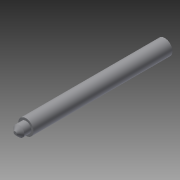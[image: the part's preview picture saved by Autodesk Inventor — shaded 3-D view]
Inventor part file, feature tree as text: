
AUTODESK INVENTOR PART (.ipt)
format: ipt  version: 2013 (Build 170138000, 138)  size: 76,800 bytes
history: native  units: in
note: dims shown in document units (in); Inventor stores cm internally (conversion verified against a paired STEP export)
features: extrude x2, sketch x2, chamfer x1
ambient origin geometry x8: Origin, YZ Plane, XZ Plane, XY Plane, X Axis, Y Axis, Z Axis, Center Point
bodies: Solid1 (feature_tree)
feature tree (5):
  extrude  "Extrusion1"  Depth=13.0in TaperAngle=0.0deg
  extrude  "Extrusion2"  Depth=1.0in TaperAngle=0.0deg
  chamfer  "Chamfer1"  Distance=0.35in Angle=45.0deg
  sketch  "Sketch1"  dims[d0=1.43in d1=13.0in d2=0.0in]
  sketch  "Sketch2"  dims[d3=1.0in d4=1.0in d5=0.0in d6=0.35in d7=0.125in d8=45.0deg]
